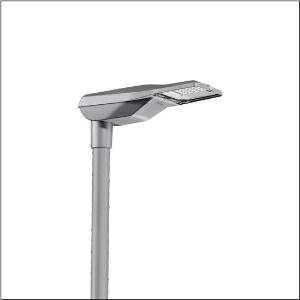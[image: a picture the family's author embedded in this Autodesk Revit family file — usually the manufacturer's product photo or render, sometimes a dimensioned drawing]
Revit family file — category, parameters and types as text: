
# Revit family: streetlight_sl_21_iq_micro___stw1_0a_5xe1e41d08db_39eb
name_source: partatom
category: Lighting Fixtures
units: mm (PartAtom-declared; Revit-internal decimal feet)

## family parameters
Cut with Voids When Loaded = No
Host = Face
Light Source = No
Part Type = Normal
Room Calculation Point = No
Round Connector Dimension = Use Diameter
Shared = No

## types (1)
- --- (1 x LED, 5010 lm, 36.4 W, 4000K)
    Apparent Load = 36 VA
    CIE Flux Codes = 38 75 98 100 100
    Color Rendering = 70
    Color Temperature = 4000K
    Default Elevation = 1800 mm
    Description = Streetlight SL 21 iQ micro, mast luminaire, primary light control with lens, of PMMA, primary optical cover: cover, of toughened safety glass, transparent, light distribution: STW1.0a, light emission: direct distribution, primary light characteristic: asymmetric, installation type: post-top, side-entry, LED, High Power LED, rated luminous flux: 5.010lm, luminous efficacy: 138lm/W, light colour: 740, colour temperature: 4000K, control gear: iQ-Comfort, control: Auto-Match, Temp-Guard, Lumen-Switch, Night-Set, Smart-Wire, Light-Fading, Desk-Remote (wireless, voltage-free reading and setting of iQ features in the workshop via application-optimized NFC function/RFID function), optimised constant luminous flux control (CLO 2.0), pre-setting: linear dimming characteristic, mains connection: 220..240V, AC, 50/60Hz, start of lifetime: 36W, end of service life: 38W, reduction: 16W, luminaire housing, of diecast aluminium, powder-coated, Siteco® metallic grey (DB 702S), corrosivity category C5 high according to DIN EN ISO 12944, please order mast flange separately, inclination adjustable: 0°, 5°, 10°, 15°, sealing non-destructively replaceable, multi-level sealing system, length: 528mm, width: 235mm, height: 110mm, mast flange for spigot size: 42mm (side-entry): 5XC10008XM4, 60/48mm (side-entry/post-top): 5XC10108XM2, 76/60mm (side-entry/post-top): 5XC10108XM1, protection rating (complete): IP66, insulation class (complete): insulation class II (safety insulation), certification: CE, ENEC, ENEC+, VDE, impact resistance: IK10, permissible operating ambient temperature for outdoor applications: -40..+50°C, standard-compliant lighting for roads and squares, packaging unit: 1 piece

Light Distribution: STW1.0a
    Height = 110 mm
    Lamp = 1 x LED
    Lamp Light Flux = 5010 lm
    Lamp Power = 36.4 W
    Lamp count = 1
    Length = 528 mm
    Luminous efficacy = 138 lm/W
    Manufacturer = Siteco
    ModVariant = No
    Model = 5XE1E41D08DB
    Number of Poles = 1
    OnlyDefault = Yes
    Power Factor = 1
    Product Name = Streetlight SL 21 iQ micro | STW1.0a
    Product group = mast luminaire | pylon top
    ProductGroupID = 6100
    Protection Class = Protection class II
    Protection Degree = IP 66
    RLX_Detail_Level = 1
    RLX_Emergency_Light_Flux = 0 lm
    RLX_Emergency_Type = 0
    RLX_Emergency_Type_DB = No
    RlxData = <blob elided: 98721 chars, md5=50c69e66>
    Socket = socket
    Standby Power = 0 W
    System Light Flux = 5010 lm
    System Power = 36 W
    Type Comments = factory setting: luminous flux: 100 % | dim-lin: 254 | 715 mA
    Type Image = l_1006881.jpg
    URL = http://relux.com
    VarID = @adj_158697
    Voltage = 0 V
    Weight = 0.00 kg
    Width = 235 mm

## geometry (parser evidence)
native form markers: Blend x4, Sweep x9
no freeform markers — native parametric forms only
